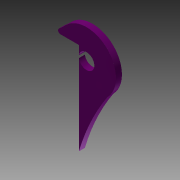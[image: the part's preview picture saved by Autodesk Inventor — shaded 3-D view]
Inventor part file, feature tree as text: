
AUTODESK INVENTOR PART (.ipt)
format: ipt  version: 2015 (Build 190159000, 159)  size: 93,184 bytes
history: native  units: mm
features: extrude x1, fillet x1, sketch x1
ambient origin geometry x8: Origin, YZ Plane, XZ Plane, XY Plane, X Axis, Y Axis, Z Axis, Center Point
bodies: Body1 (feature_tree)
feature tree (3):
  extrude  "Extrusion2"  Depth=1.0mm
  fillet  "Fillet1"  [1 undecoded]
  sketch  "Sketch1"  dims[d3=2.5mm d4=0.0mm d5=1.0mm]
note: 1 required parameter value undecoded (feature->parameter linkage not recoverable at this tier; creation-order binding heuristic only, values carry confidence <= 0.55)
